# Revit family: Air & Dirt Seperator 1124
name_source: partatom
category: Rohrzubehör
revit_build: Autodesk Revit 2018 (Build: 20190510_1515(x64)
units: mm (PartAtom-declared; Revit-internal decimal feet)

## family parameters
Arbeitsebenenbasiert = Nein
Beim Laden mit Abzugskörper schneiden = Nein
Bemaßung runder Anschluss = Durchmesser verwenden
Gemeinsam genutzt = Nein
Immer vertikal = Ja
OmniClass-Nummer = 23.65.55.14
OmniClass-Titel = Valves for Liquid Services
Teiletyp = Unterbricht

## types (1)
- Air & Dirt Seperator 1124
    Description = for installation in the heating or cooling circuit to filter out dirt and sludge particles and bleed off air.
this prevents malfunctions and damage to heating and cooling systems.
a high efficiency for the whole heating or cooling system is ensured.
the air and dirt separator is used for the separation of dirt particles and air from the heating or cooling system.
for the air separation the air and dirt separator has an air vent.
if air is present in the system, it rises to the highest point of the air and dirt separator.
the water level drops locally there, the integrated float pulls the float arm downwards and thus opens the sealing area.
the air escapes, the water level rises again and the sealing area is closed.
    H01 = 158.5 mm  [stored 0.520013 ft]
    H02 = 92.5 mm  [stored 0.303478 ft]
    H03 = 10 mm  [stored 0.0328084 ft]
    H04 = 13.7 mm  [stored 0.0449475 ft]
    H05 = 66 mm  [stored 0.216535 ft]
    H06 = 56 mm  [stored 0.183727 ft]
    H07 = 24 mm  [stored 0.0787402 ft]
    H08 = 17 mm
    H09 = 13.3 mm  [stored 0.0436352 ft]
    H10 = 46 mm  [stored 0.150919 ft]
    H11 = 122 mm  [stored 0.400262 ft]
    H12 = 45.2 mm  [stored 0.148294 ft]
    H13 = 79.8 mm  [stored 0.261811 ft]
    Hersteller = Herz-Armaturen GmbH
    L01 = 61.9 mm  [stored 0.203084 ft]
    L02 = 70 mm  [stored 0.229659 ft]
    L03 = 102 mm  [stored 0.334646 ft]
    L04 = 49 mm  [stored 0.160761 ft]
    Material = DZR brass
    Medium = water purity in accordance with the ÖNORM H 5195 and VDI 2035 standards
    R01 = 50.5 mm  [stored 0.165682 ft]
    R02 = 43.5 mm  [stored 0.142717 ft]
    R03 = 14 mm  [stored 0.0459318 ft]
    R04 = 8.3 mm  [stored 0.027231 ft]
    R05 = 29 mm  [stored 0.0951444 ft]
    R06 = 21 mm  [stored 0.0688976 ft]
    R07 = 17 mm
    R08 = 34 mm
    R09 = 27.5 mm  [stored 0.0902231 ft]
    R10 = 20 mm  [stored 0.0656168 ft]
    R80 = 20 mm  [stored 0.0656168 ft]
    R90 = 1 mm  [stored 0.00328084 ft]
    R91 = 20.7 mm  [stored 0.0679134 ft]
    R92 = 5 mm  [stored 0.0164042 ft]
    S01 = 33.1 mm  [stored 0.108596 ft]
    S02 = 112 mm  [stored 0.367454 ft]
    S03 = 86 mm  [stored 0.282152 ft]
    S04 = 112.9 mm  [stored 0.370407 ft]
    SCRNCODE = 05;14;02
    SCRNSEQ = AWI;AWI_TYP="1016";2
    T01 = 43 mm  [stored 0.141076 ft]
    URL = www.herzvalves.com
    VRL01 = 30 mm  [stored 0.0984252 ft]
    VRL02 = 13 mm
    VRL03 = 18 mm  [stored 0.0590551 ft]
    VRL04 = 8 mm  [stored 0.0262467 ft]
    VRL05 = 17 mm
    Work pressure = 1000000.0 Pa
    max. Operating pressure = 1000000.0 Pa
    max. Operating temperature (without steam) = 110 °C

note: [stored X ft] marks values corroborated as IEEE doubles in the binary element streams (Revit-internal decimal feet)
